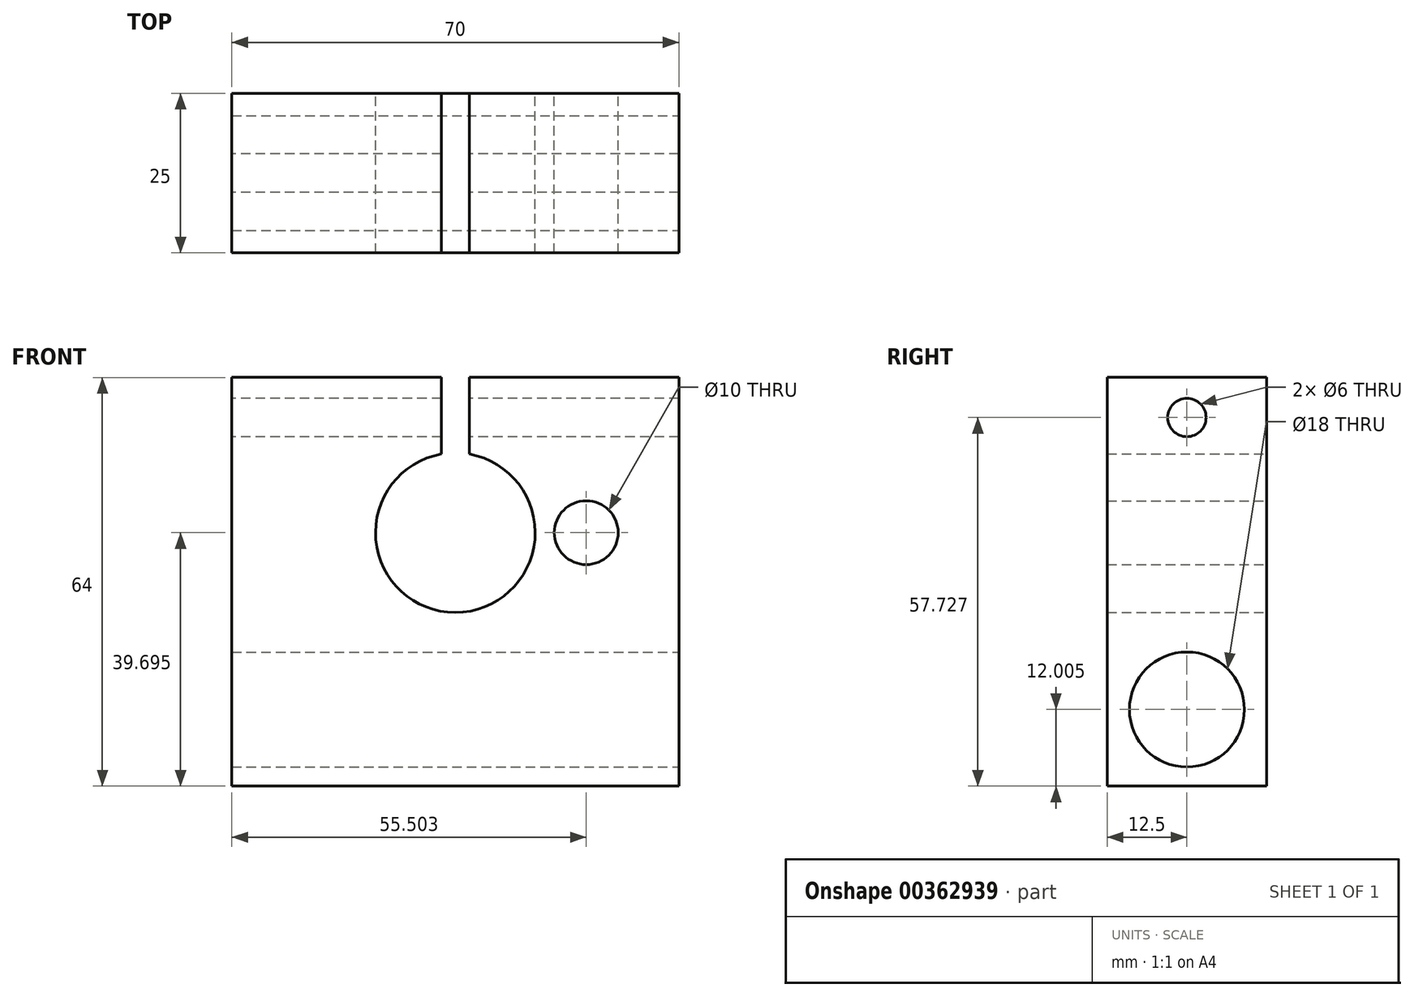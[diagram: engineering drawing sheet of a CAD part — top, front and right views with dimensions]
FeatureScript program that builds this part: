
annotation { "Feature Type Name" : "Feature", "Feature Type Description" : "" }
export const myFeature = defineFeature(function(context is Context, id is Id, definition is map)
    precondition{}
    {
        {
            var Q0;
            Q0=qCreatedBy(makeId("Front.planeOp"),FACE);
            var sketch = newSketch(context, id + "F0", { "sketchPlane" : qUnion([Q0])});
            skLineSegment(sketch, "E0", {"start": v(20.56, 15.02) * mm, "end": v(41.06, 15.02) * mm, "construction": true});
            skArc(sketch, "E1", {"start": v(18.39, 27.32) * mm, "mid": v(20.56, 2.52) * mm, "end": v(22.74, 27.32) * mm});
            skLineSegment(sketch, "E2", {"start": v(20.56, 15.02) * mm, "end": v(20.56, -38.62) * mm, "construction": true});
            skLineSegment(sketch, "E3", {"start": v(-14.44, -24.68) * mm, "end": v(-14.44, 39.32) * mm});
            skLineSegment(sketch, "E4", {"start": v(-14.44, 39.32) * mm, "end": v(18.39, 39.32) * mm});
            skLineSegment(sketch, "E5.MirrorCS", {"start": v(55.56, -24.68) * mm, "end": v(55.56, 39.32) * mm});
            skLineSegment(sketch, "E6.MirrorCS", {"start": v(55.56, 39.32) * mm, "end": v(22.74, 39.32) * mm});
            skLineSegment(sketch, "E7", {"start": v(20.56, -24.68) * mm, "end": v(55.56, -24.68) * mm});
            skLineSegment(sketch, "E8", {"start": v(18.39, 27.32) * mm, "end": v(18.39, 39.32) * mm});
            skLineSegment(sketch, "E9.MirrorCS", {"start": v(22.74, 27.32) * mm, "end": v(22.74, 39.32) * mm});
            skCircle(sketch, "E10", {"center": v(41.06, 15.02) * mm, "radius": 5 * mm});
            skLineSegment(sketch, "E11.MirrorCS", {"start": v(20.56, -24.68) * mm, "end": v(-14.44, -24.68) * mm});
            skArc(sketch, "E12.MirrorCS", {"start": v(22.74, 27.32) * mm, "mid": v(20.56, 2.52) * mm, "end": v(18.39, 27.32) * mm});
            skSolve(sketch);
        }
        {
            var Q0;
            Q0 = qSketchRegion(id + "F0", true);
            extrude(context, id + "F1", {"entities" : qUnion([Q0]), "depth" : 25 * mm});
        }
        {
            var Q0;
            Q0=makeQuery(id+"F1.opExtrude","SWEPT_FACE",FACE,{"disambiguationData":[OSD([sQuery(id+"F0.wireOp",EDGE,"E3")])]});
            var sketch = newSketch(context, id + "F2", { "sketchPlane" : qUnion([Q0])});
            skCircle(sketch, "E13", {"center": v(12.5, 33.05) * mm, "radius": 2.5 * mm});
            skSolve(sketch);
        }
        {
            var Q0;
            Q0=sQuery(id+"F2.wireOp",VERTEX,"E13.center");
            var Q1;
            Q1=makeQuery(id+"F1.opExtrude","SWEPT_BODY",BODY,{"disambiguationData":[OSD([sQuery(id+"F0.wireOp",EDGE,"E3"),sQuery(id+"F0.wireOp",EDGE,"E4"),sQuery(id+"F0.wireOp",EDGE,"E5.MirrorCS"),sQuery(id+"F0.wireOp",EDGE,"E6.MirrorCS"),sQuery(id+"F0.wireOp",EDGE,"E7"),sQuery(id+"F0.wireOp",EDGE,"E8"),sQuery(id+"F0.wireOp",EDGE,"E9.MirrorCS"),sQuery(id+"F0.wireOp",EDGE,"E10"),sQuery(id+"F0.wireOp",EDGE,"E12.MirrorCS"),sQuery(id+"F0.wireOp",EDGE,"E11.MirrorCS")])]});
            hole(context, id + "F3", {"style" : HoleStyle.SIMPLE, "endStyle" : HoleEndStyle.THROUGH, "holeDiameter" : 6 * mm, "isTappedThrough" : true, "tappedDepth" : 12 * mm, "tapClearance" : 3, "locations" : qUnion([Q0]), "scope" : qUnion([Q1])});
        }
        {
            var Q0;
            Q0=makeQuery(id+"F1.opExtrude","SWEPT_FACE",FACE,{"disambiguationData":[OSD([sQuery(id+"F0.wireOp",EDGE,"E5.MirrorCS")])]});
            var sketch = newSketch(context, id + "F4", { "sketchPlane" : qUnion([Q0])});
            skCircle(sketch, "E14", {"center": v(-12.5, -12.68) * mm, "radius": 9 * mm});
            skSolve(sketch);
        }
        {
            var Q0;
            Q0=sQuery(id+"F4.wireOp",VERTEX,"E14.center");
            var Q1;
            Q1=makeQuery(id+"F1.opExtrude","SWEPT_BODY",BODY,{"disambiguationData":[OSD([sQuery(id+"F0.wireOp",EDGE,"E3"),sQuery(id+"F0.wireOp",EDGE,"E4"),sQuery(id+"F0.wireOp",EDGE,"E5.MirrorCS"),sQuery(id+"F0.wireOp",EDGE,"E6.MirrorCS"),sQuery(id+"F0.wireOp",EDGE,"E7"),sQuery(id+"F0.wireOp",EDGE,"E8"),sQuery(id+"F0.wireOp",EDGE,"E9.MirrorCS"),sQuery(id+"F0.wireOp",EDGE,"E10"),sQuery(id+"F0.wireOp",EDGE,"E12.MirrorCS"),sQuery(id+"F0.wireOp",EDGE,"E11.MirrorCS")])]});
            hole(context, id + "F5", {"style" : HoleStyle.SIMPLE, "endStyle" : HoleEndStyle.THROUGH, "holeDiameter" : 18 * mm, "isTappedThrough" : true, "tappedDepth" : 12 * mm, "tapClearance" : 3, "locations" : qUnion([Q0]), "scope" : qUnion([Q1])});
        }
    });
